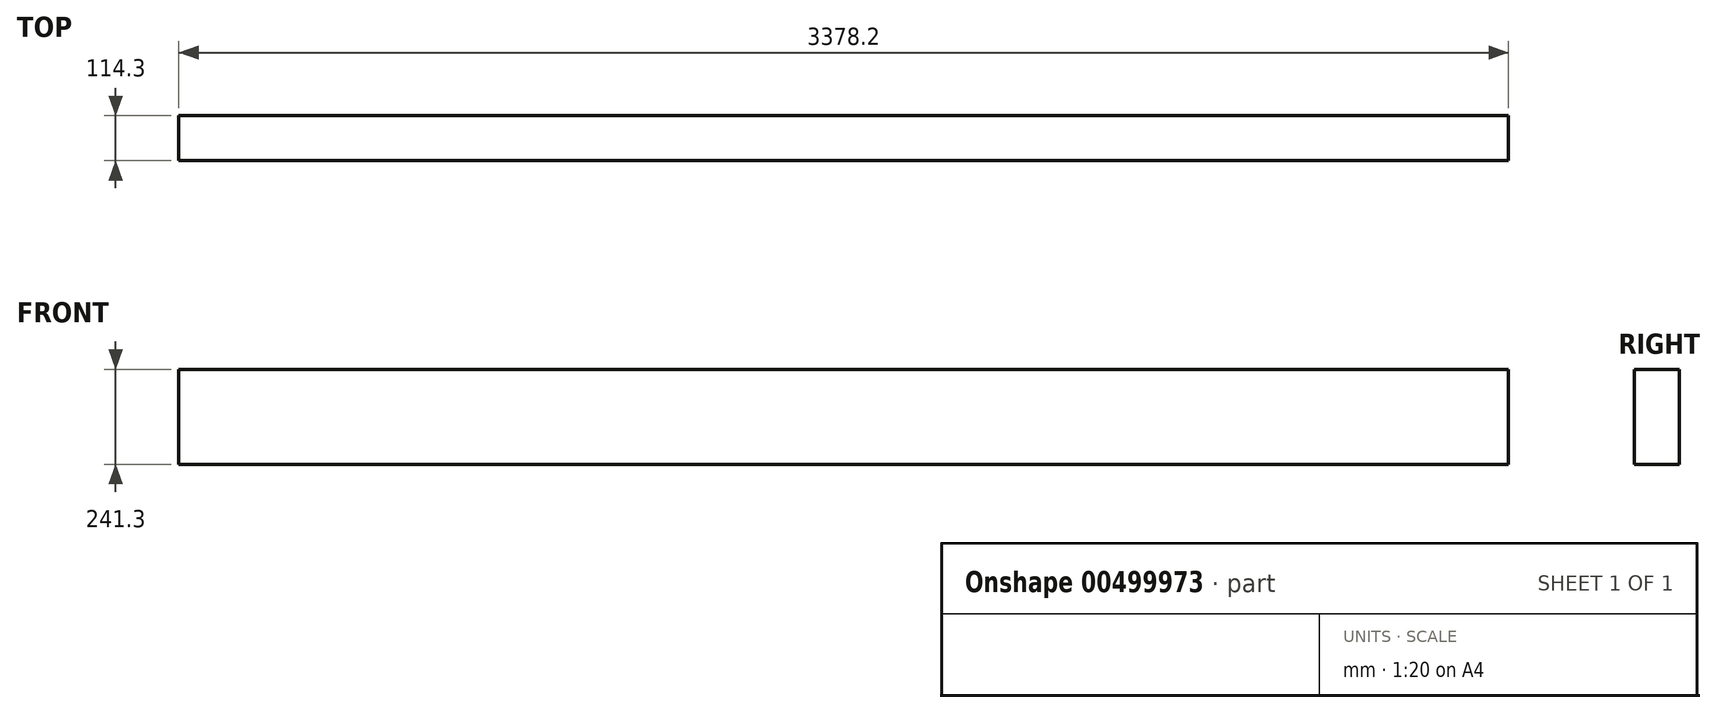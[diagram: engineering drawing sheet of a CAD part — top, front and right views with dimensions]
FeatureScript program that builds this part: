
annotation { "Feature Type Name" : "Feature", "Feature Type Description" : "" }
export const myFeature = defineFeature(function(context is Context, id is Id, definition is map)
    precondition{}
    {
        {
            var Q0;
            Q0=qCreatedBy(makeId("Front.planeOp"),FACE);
            var sketch = newSketch(context, id + "F0", { "sketchPlane" : qUnion([Q0])});
            skLineSegment(sketch, "E0.bottom", {"start": v(-1689.1, 120.65) * mm, "end": v(1689.1, 120.65) * mm});
            skLineSegment(sketch, "E0.top", {"start": v(-1689.1, -120.65) * mm, "end": v(1689.1, -120.65) * mm});
            skLineSegment(sketch, "E0.left", {"start": v(-1689.1, 120.65) * mm, "end": v(-1689.1, -120.65) * mm});
            skLineSegment(sketch, "E0.right", {"start": v(1689.1, 120.65) * mm, "end": v(1689.1, -120.65) * mm});
            skPoint(sketch, "E0.middle", {"position": v(0, 0) * mm});
            skSolve(sketch);
        }
        {
            var Q0;
            Q0 = qSketchRegion(id + "F0", true);
            extrude(context, id + "F1", {"entities" : qUnion([Q0]), "depth" : 114.3 * mm, "offsetDistance" : 25.4 * mm});
        }
    });
